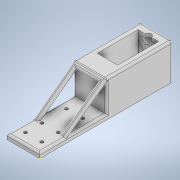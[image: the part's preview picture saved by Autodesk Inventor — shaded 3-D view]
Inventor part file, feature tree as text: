
AUTODESK INVENTOR PART (.ipt)
format: ipt  version: 2021 (Build 250183000, 183)  size: 346,112 bytes
history: native  units: mm
features: extrude x15, sketch x15, fillet x2, other x1
ambient origin geometry x8: Origin, YZ Plane, XZ Plane, XY Plane, X Axis, Y Axis, Z Axis, Center Point
bodies: Body1 (feature_tree)
feature tree (33):
  other  "Sólido1"
  extrude  "Extrusión1"  Depth=5.0mm
  extrude  "Extrusión3"  Depth=15.0mm
  extrude  "Extrusión4"  Depth=32.0mm TaperAngle=0.0deg
  extrude  "Extrusión8"  Depth=40.0mm TaperAngle=0.0deg
  extrude  "Extrusión9"  Depth=10.0mm TaperAngle=0.0deg
  extrude  "Extrusión10"  Depth=10.0mm
  extrude  "Extrusión11"  Depth=5.0mm
  extrude  "Extrusión13"  Depth=5.0mm TaperAngle=0.0deg
  extrude  "Extrusión15"  Depth=2.0mm TaperAngle=0.0deg
  fillet  "Empalme1"  Radius=10.0mm
  extrude  "Extrusión18"  Depth=2.0mm
  fillet  "Empalme2"  Radius=3.0mm
  sketch  "Boceto25"  dims[d188=10.0mm d189=3.0mm]
  extrude  "Extrusión16"  Depth=3.0mm
  sketch  "Boceto26"  dims[d190=6.0mm d191=3.0mm]
  sketch  "Boceto27"  dims[d192=7.0mm d193=6.0mm]
  extrude  "Extrusión19"  Depth=3.0mm
  extrude  "Extrusión20"  Depth=6.0mm
  extrude  "Extrusión21"  Depth=35.0mm TaperAngle=0.0deg
  extrude  "Extrusión22"  Depth=3.0mm
  sketch  "Boceto1"  dims[d22=5.0mm d23=0.0mm d33=50.0mm]
  sketch  "Boceto3"  dims[d35=50.0mm d37=15.0mm]
  sketch  "Boceto4"  dims[d38=25.0mm d39=32.0mm d40=0.0mm]
  sketch  "Boceto8"  dims[d41=50.0mm d42=0.0mm d62=40.0mm d63=0.0mm]
  sketch  "Boceto9"  dims[d76=10.0mm d77=40.0mm d78=0.0mm]
  sketch  "Boceto10"  dims[d79=40.0mm d80=0.0mm d81=10.0mm]
  sketch  "Boceto11"  dims[d82=40.0mm d83=0.0mm d89=5.0mm]
  sketch  "Boceto13"  dims[d90=5.0mm d107=40.0mm d108=0.0mm]
  sketch  "Boceto20"  dims[d139=400.0mm d140=0.0mm d166=1.0mm d167=0.0mm d176=10.0mm d180=2.0mm]
  sketch  "Boceto24"  dims[d184=39.0mm d185=0.0mm d186=2.0mm d187=3.0mm]
  sketch  "Boceto28"  dims[d194=100.0mm d195=0.0mm d196=35.0mm d197=0.0mm]
  sketch  "Boceto29"  dims[d198=35.0mm d199=0.0mm d224=3.0mm d225=3.0mm d226=3.0mm d227=3.0mm d228=3.0mm d229=3.0mm d230=10.0mm d231=0.0mm d103=0.5mm d104=0.872665mm d105=0.5mm d106=0.872665mm d154=0.5mm d155=0.872665mm d156=0.5mm d157=0.872665mm]
